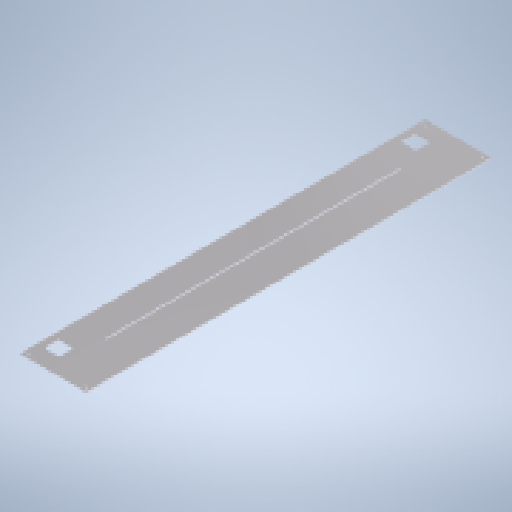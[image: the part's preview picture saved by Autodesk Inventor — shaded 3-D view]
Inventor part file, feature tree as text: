
AUTODESK INVENTOR PART (.ipt)
format: ipt  version: 2025 (Build 290162010, 162A)  size: 224,256 bytes
history: native  units: mm
features: sketch x3, extrude x2, hole x1, other x1
ambient origin geometry x8: Origin, YZ Plane, XZ Plane, XY Plane, X Axis, Y Axis, Z Axis, Center Point
bodies: Volumenkörper1 (feature_tree)
feature tree (7):
  extrude  "Extrusion1"  Depth=40.0mm
  extrude  "Extrusion2"  Depth=525.0mm
  hole  "Bohrung1"  [1 undecoded]
  sketch  "Skizze1"  dims[d0=3.0mm d1=40.0mm]
  sketch  "Skizze2"  dims[d2=40.249122mm d3=525.0mm]
  sketch  "Skizze3"  dims[d4=0.0mm d5=0.0mm d6=16.712001mm d8=51.636694mm d9=525.0mm d10=4.0mm d14=98.05mm d15=800.0mm d16=20.0mm d17=40.0mm d18=45.0mm d19=1.0mm d20=0.0mm d21=0.0mm d22=12.0mm d23=4.3mm d24=5.0mm d25=9.4mm d26=2.0mm d27=15.7mm d28=6.3mm d29=20.594885mm d7=0.15mm d11=0.75mm d12=1180.0mm d13=0.0625mm]
  other  "item_0047308_Blech Al 2mm_L=1100_B=180_1"
note: 1 required parameter value undecoded (feature->parameter linkage not recoverable at this tier; creation-order binding heuristic only, values carry confidence <= 0.55)
